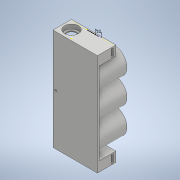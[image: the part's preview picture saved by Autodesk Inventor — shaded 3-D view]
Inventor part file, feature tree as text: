
AUTODESK INVENTOR PART (.ipt)
format: ipt  version: 2020 (Build 240168000, 168)  size: 734,208 bytes
history: native  units: mm
features: sketch x25, extrude x22, fillet x4
ambient origin geometry x8: Origin, YZ Plane, XZ Plane, XY Plane, X Axis, Y Axis, Z Axis, Center Point
bodies: Solid1 (feature_tree)
feature tree (51):
  extrude  "Extrusion1"  Depth=165.0mm
  extrude  "Extrusion2"  Depth=8.5mm
  extrude  "Extrusion3"  Depth=25.0mm TaperAngle=0.0deg
  extrude  "Extrusion4"  Depth=22.75mm
  extrude  "Extrusion5"  Depth=15.5mm
  extrude  "Extrusion6"  Depth=7.1mm TaperAngle=0.0deg
  fillet  "Fillet1"  Radius=5.0mm
  extrude  "Extrusion7"  Depth=10.0mm TaperAngle=0.0deg
  fillet  "Fillet2"  Radius=2.0mm
  extrude  "Extrusion8"  Depth=16.0mm
  extrude  "Extrusion9"  Depth=16.0mm
  fillet  "Fillet3"  Radius=8.0mm
  extrude  "Extrusion10"  Depth=6.0mm
  extrude  "Extrusion11"  Depth=12.25mm
  sketch  "Sketch12"  dims[d32=12.25mm d33=3.5mm]
  sketch  "Sketch13"  dims[d34=12.25mm d35=12.25mm]
  extrude  "Extrusion12"  Depth=12.25mm
  extrude  "Extrusion13"  Depth=12.25mm
  sketch  "Sketch16"  dims[d41=8.0mm d42=1.0mm]
  extrude  "Extrusion14"  Depth=40.0mm TaperAngle=0.0deg
  extrude  "Extrusion15"  Depth=2.0mm
  extrude  "Extrusion16"  Depth=1.0mm
  extrude  "Extrusion17"  Depth=2.0mm TaperAngle=0.0deg
  extrude  "Extrusion18"  Depth=7.1mm TaperAngle=0.0deg
  fillet  "Fillet4"  Radius=3.0mm
  extrude  "Extrusion19"  Depth=42.0mm
  extrude  "Extrusion20"  Depth=42.0mm
  extrude  "Extrusion21"  Depth=42.0mm
  extrude  "Extrusion22"  Depth=2.0mm
  sketch  "Sketch1"  dims[d0=25.0mm d1=165.0mm]
  sketch  "Sketch2"  dims[d2=3.0mm d3=0.0mm d4=8.5mm]
  sketch  "Sketch3"  dims[d5=8.5mm d6=25.0mm d7=0.0mm]
  sketch  "Sketch4"  dims[d8=25.0mm d9=22.75mm]
  sketch  "Sketch5"  dims[d10=7.1mm d11=0.0mm d12=15.5mm]
  sketch  "Sketch6"  dims[d13=165.0mm d14=0.0mm d15=7.1mm d16=0.0mm d17=5.0mm]
  sketch  "Sketch7"  dims[d18=5.0mm d19=10.0mm d20=0.0mm d21=2.0mm]
  sketch  "Sketch8"  dims[d22=16.0mm d23=8.0mm]
  sketch  "Sketch9"  dims[d24=16.0mm d25=16.0mm d26=8.0mm]
  sketch  "Sketch10"  dims[d27=45.0mm d28=0.0mm d29=6.0mm]
  sketch  "Sketch11"  dims[d30=12.25mm d31=3.5mm]
  sketch  "Sketch14"  dims[d36=3.5mm d37=40.0mm d38=0.0mm]
  sketch  "Sketch15"  dims[d39=1.0mm d40=2.0mm]
  sketch  "Sketch17"  dims[d43=2.0mm d44=12.0mm d45=0.0mm]
  sketch  "Sketch18"  dims[d46=6.0mm d47=7.1mm d48=0.0mm d49=3.0mm d50=0.0mm]
  sketch  "Sketch19"  dims[d51=42.0mm d52=38.75mm]
  sketch  "Sketch20"  dims[d53=42.0mm d54=38.75mm]
  sketch  "Sketch21"  dims[d55=42.0mm d56=38.75mm]
  sketch  "Sketch22"  dims[d57=45.0mm d58=0.0mm d59=2.0mm]
  sketch  "Sketch23"  dims[d60=4.0mm]
  sketch  "Sketch24"  dims[d61=2.0mm]
  sketch  "Sketch25"  dims[d62=4.0mm d63=45.0mm d64=0.0mm d65=10.0mm d66=12.0mm d67=0.0mm d68=2.0mm d69=0.0mm d70=2.0mm d71=0.0mm d72=2.0mm d73=2.0mm d74=5.0mm d75=0.0mm d76=2.0mm d77=2.0mm d78=7.0mm d79=0.0mm d80=1.0mm d81=0.25mm d82=0.25mm d83=44.75mm d84=0.0mm d85=44.0mm d86=0.0mm d87=22.6mm d88=8.5mm d89=0.0mm d90=22.6mm d91=8.5mm d92=0.0mm]
